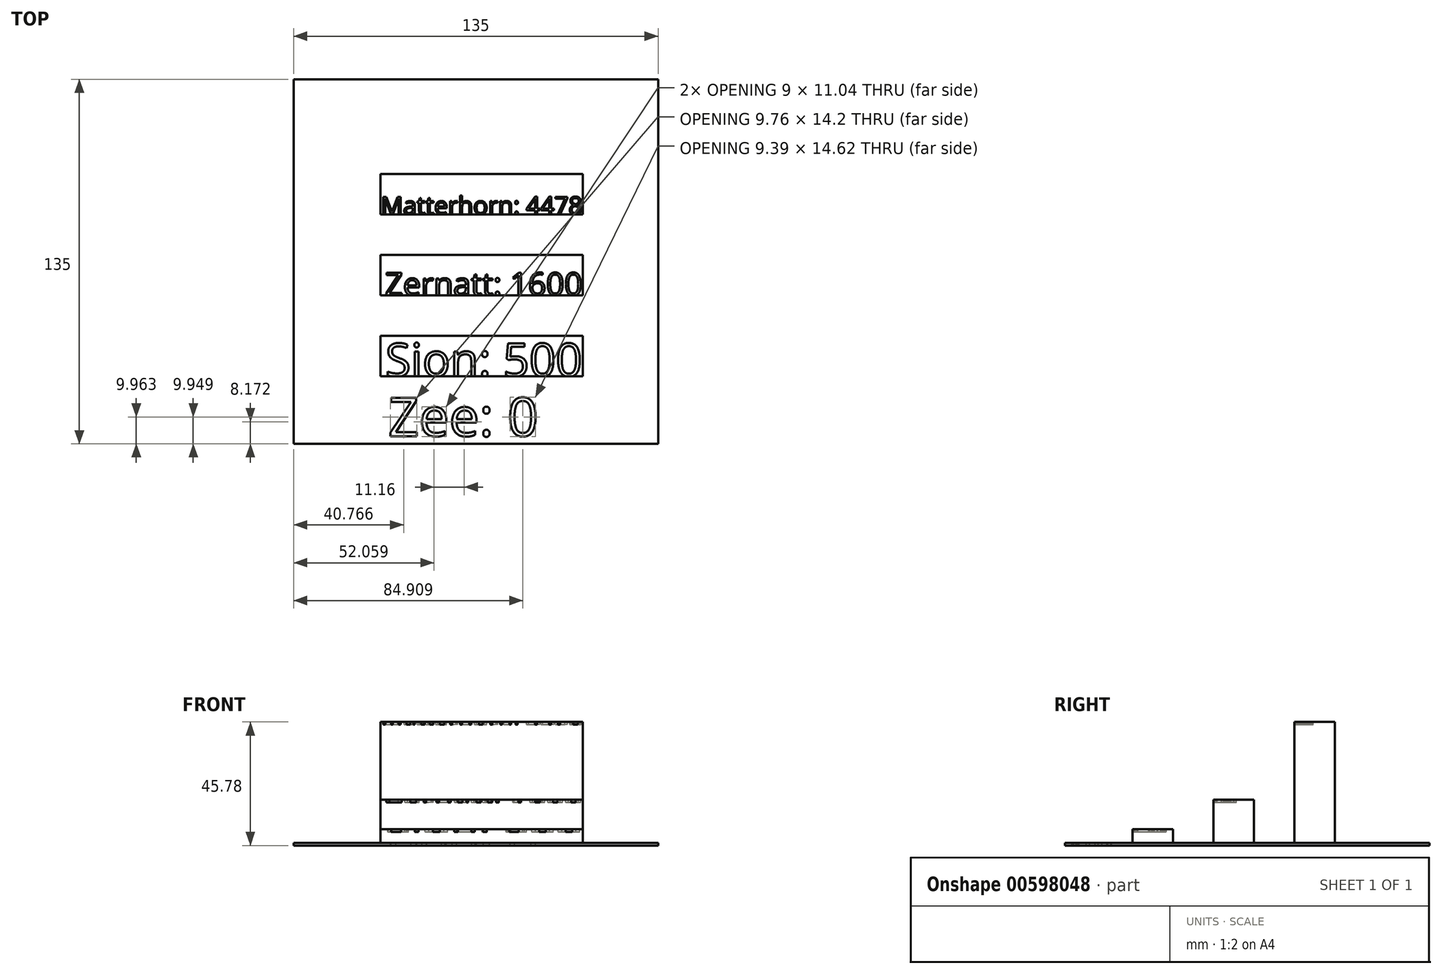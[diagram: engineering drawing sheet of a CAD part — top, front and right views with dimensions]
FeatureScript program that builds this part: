
annotation { "Feature Type Name" : "Feature", "Feature Type Description" : "" }
export const myFeature = defineFeature(function(context is Context, id is Id, definition is map)
    precondition{}
    {
        {
            var Q0;
            Q0=qCreatedBy(makeId("Top.planeOp"),FACE);
            var sketch = newSketch(context, id + "F0", { "sketchPlane" : qUnion([Q0])});
            skLineSegment(sketch, "E0.bottom", {"start": v(-68.73, 68.01) * mm, "end": v(66.27, 68.01) * mm});
            skLineSegment(sketch, "E0.top", {"start": v(-68.73, -66.99) * mm, "end": v(66.27, -66.99) * mm});
            skLineSegment(sketch, "E0.left", {"start": v(-68.73, 68.01) * mm, "end": v(-68.73, -66.99) * mm});
            skLineSegment(sketch, "E0.right", {"start": v(66.27, 68.01) * mm, "end": v(66.27, -66.99) * mm});
            skSolve(sketch);
        }
        {
            var Q0;
            Q0=makeQuery(id+"F0.imprint","IMPRINT",FACE,{"disambiguationData":[TD([[makeQuery(id+"F0.imprint","IMPRINT",EDGE,{"derivedFrom":sQuery(id+"F0.wireOp",EDGE,"E0.bottom")}),-1.0]])]});
            extrude(context, id + "F1", {"entities" : qUnion([Q0]), "depth" : 1 * mm, "offsetDistance" : 25 * mm});
        }
        {
            var Q0;
            Q0=makeQuery(id+"F1.opExtrude","CAP_FACE",FACE,{"disambiguationData":[OSD([sQuery(id+"F0.wireOp",EDGE,"E0.bottom"),sQuery(id+"F0.wireOp",EDGE,"E0.top"),sQuery(id+"F0.wireOp",EDGE,"E0.left"),sQuery(id+"F0.wireOp",EDGE,"E0.right")])],"isStart":false});
            var sketch = newSketch(context, id + "F2", { "sketchPlane" : qUnion([Q0])});
            skLineSegment(sketch, "E1.bottom", {"start": v(-36.6, -26.99) * mm, "end": v(38.4, -26.99) * mm});
            skLineSegment(sketch, "E1.top", {"start": v(-36.6, -41.99) * mm, "end": v(38.4, -41.99) * mm});
            skLineSegment(sketch, "E1.left", {"start": v(-36.6, -26.99) * mm, "end": v(-36.6, -41.99) * mm});
            skLineSegment(sketch, "E1.right", {"start": v(38.4, -26.99) * mm, "end": v(38.4, -41.99) * mm});
            skSolve(sketch);
        }
        {
            var Q0;
            Q0=makeQuery(id+"F2.imprint","IMPRINT",FACE,{"disambiguationData":[TD([[makeQuery(id+"F2.imprint","IMPRINT",EDGE,{"derivedFrom":sQuery(id+"F2.wireOp",EDGE,"E1.bottom")}),1.0]])]});
            var sketch = newSketch(context, id + "F3", { "sketchPlane" : qUnion([Q0])});
            skLineSegment(sketch, "E2.bottom", {"start": v(-36.6, 3.01) * mm, "end": v(38.4, 3.01) * mm});
            skLineSegment(sketch, "E2.top", {"start": v(-36.6, -11.99) * mm, "end": v(38.4, -11.99) * mm});
            skLineSegment(sketch, "E2.left", {"start": v(-36.6, 3.01) * mm, "end": v(-36.6, -11.99) * mm});
            skLineSegment(sketch, "E2.right", {"start": v(38.4, 3.01) * mm, "end": v(38.4, -11.99) * mm});
            skSolve(sketch);
        }
        {
            var Q0;
            Q0=makeQuery(id+"F2.imprint","IMPRINT",FACE,{"disambiguationData":[TD([[makeQuery(id+"F2.imprint","IMPRINT",EDGE,{"derivedFrom":sQuery(id+"F2.wireOp",EDGE,"E1.bottom")}),1.0]])]});
            var sketch = newSketch(context, id + "F4", { "sketchPlane" : qUnion([Q0])});
            skLineSegment(sketch, "E3.bottom", {"start": v(-36.6, 33.01) * mm, "end": v(38.4, 33.01) * mm});
            skLineSegment(sketch, "E3.top", {"start": v(-36.6, 18.01) * mm, "end": v(38.4, 18.01) * mm});
            skLineSegment(sketch, "E3.left", {"start": v(-36.6, 33.01) * mm, "end": v(-36.6, 18.01) * mm});
            skLineSegment(sketch, "E3.right", {"start": v(38.4, 33.01) * mm, "end": v(38.4, 18.01) * mm});
            skSolve(sketch);
        }
        {
            var Q0;
            Q0=makeQuery(id+"F2.imprint","IMPRINT",FACE,{"disambiguationData":[TD([[makeQuery(id+"F2.imprint","IMPRINT",EDGE,{"derivedFrom":sQuery(id+"F2.wireOp",EDGE,"E1.bottom")}),-1.0]])]});
            extrude(context, id + "F5", {"entities" : qUnion([Q0]), "operationType" : NewBodyOperationType.ADD, "depth" : 5 * mm, "offsetDistance" : 25 * mm});
        }
        {
            var Q0;
            Q0=makeQuery(id+"F3.imprint","IMPRINT",FACE,{"disambiguationData":[TD([[makeQuery(id+"F3.imprint","IMPRINT",EDGE,{"derivedFrom":sQuery(id+"F3.wireOp",EDGE,"E2.bottom")}),-1.0]])]});
            extrude(context, id + "F6", {"entities" : qUnion([Q0]), "operationType" : NewBodyOperationType.ADD, "depth" : 16 * mm, "offsetDistance" : 25 * mm});
        }
        {
            var Q0;
            Q0=makeQuery(id+"F4.imprint","IMPRINT",FACE,{"disambiguationData":[TD([[makeQuery(id+"F4.imprint","IMPRINT",EDGE,{"derivedFrom":sQuery(id+"F4.wireOp",EDGE,"E3.bottom")}),-1.0]])]});
            extrude(context, id + "F7", {"entities" : qUnion([Q0]), "operationType" : NewBodyOperationType.ADD, "depth" : 44.78 * mm, "offsetDistance" : 25 * mm});
        }
        {
            var Q0;
            Q0=makeQuery(id+"F7.opExtrude","CAP_FACE",FACE,{"disambiguationData":[OSD([sQuery(id+"F4.wireOp",EDGE,"E3.bottom"),sQuery(id+"F4.wireOp",EDGE,"E3.top"),sQuery(id+"F4.wireOp",EDGE,"E3.left"),sQuery(id+"F4.wireOp",EDGE,"E3.right")])],"isStart":false});
            var sketch = newSketch(context, id + "F8", { "sketchPlane" : qUnion([Q0])});
            skText(sketch, "E4", { "text": "Matterhorn: 4478", "fontName": "OpenSans-Regular.ttf"});
            const initialGuessF8  = {"E4": [-0.03642, 0.01801, 1, 0, 0.00657]};
            skSetInitialGuess(sketch, initialGuessF8);
            skSolve(sketch);
        }
        {
            var Q0;
            Q0=makeQuery(id+"F6.opExtrude","CAP_FACE",FACE,{"disambiguationData":[OSD([sQuery(id+"F3.wireOp",EDGE,"E2.bottom"),sQuery(id+"F3.wireOp",EDGE,"E2.top"),sQuery(id+"F3.wireOp",EDGE,"E2.left"),sQuery(id+"F3.wireOp",EDGE,"E2.right")])],"isStart":false});
            var sketch = newSketch(context, id + "F9", { "sketchPlane" : qUnion([Q0])});
            skText(sketch, "E5", { "text": "Zernatt: 1600", "fontName": "OpenSans-Regular.ttf"});
            const initialGuessF9  = {"E5": [-0.03488, -0.01199, 1, 0, 0.00845]};
            skSetInitialGuess(sketch, initialGuessF9);
            skSolve(sketch);
        }
        {
            var Q0;
            Q0=makeQuery(id+"F5.opExtrude","CAP_FACE",FACE,{"disambiguationData":[OSD([sQuery(id+"F2.wireOp",EDGE,"E1.bottom"),sQuery(id+"F2.wireOp",EDGE,"E1.top"),sQuery(id+"F2.wireOp",EDGE,"E1.left"),sQuery(id+"F2.wireOp",EDGE,"E1.right")])],"isStart":false});
            var sketch = newSketch(context, id + "F10", { "sketchPlane" : qUnion([Q0])});
            skText(sketch, "E6", { "text": "Sion: 500", "fontName": "OpenSans-Regular.ttf"});
            const initialGuessF10  = {"E6": [-0.03472, -0.04199, 1, 0, 0.01231]};
            skSetInitialGuess(sketch, initialGuessF10);
            skSolve(sketch);
        }
        {
            var Q0;
            Q0=makeQuery(id+"F1.opExtrude","CAP_FACE",FACE,{"disambiguationData":[OSD([sQuery(id+"F0.wireOp",EDGE,"E0.bottom"),sQuery(id+"F0.wireOp",EDGE,"E0.top"),sQuery(id+"F0.wireOp",EDGE,"E0.left"),sQuery(id+"F0.wireOp",EDGE,"E0.right")])],"isStart":false});
            var sketch = newSketch(context, id + "F11", { "sketchPlane" : qUnion([Q0])});
            skText(sketch, "E7", { "text": "Zee: 0", "fontName": "OpenSans-Regular.ttf"});
            const initialGuessF11  = {"E7": [-0.03364, -0.06414, 1, 0, 0.01432]};
            skSetInitialGuess(sketch, initialGuessF11);
            skSolve(sketch);
        }
        {
            var Q0;
            Q0 = qSketchRegion(id + "F8", true);
            var Q1;
            Q1 = qSketchRegion(id + "F9", true);
            var Q2;
            Q2 = qSketchRegion(id + "F10", true);
            var Q3;
            Q3 = qSketchRegion(id + "F11", true);
            extrude(context, id + "F12", {"entities" : qUnion([Q0, Q1, Q2, Q3]), "operationType" : NewBodyOperationType.REMOVE, "oppositeDirection" : true, "depth" : 1 * mm, "offsetDistance" : 25 * mm});
        }
    });
